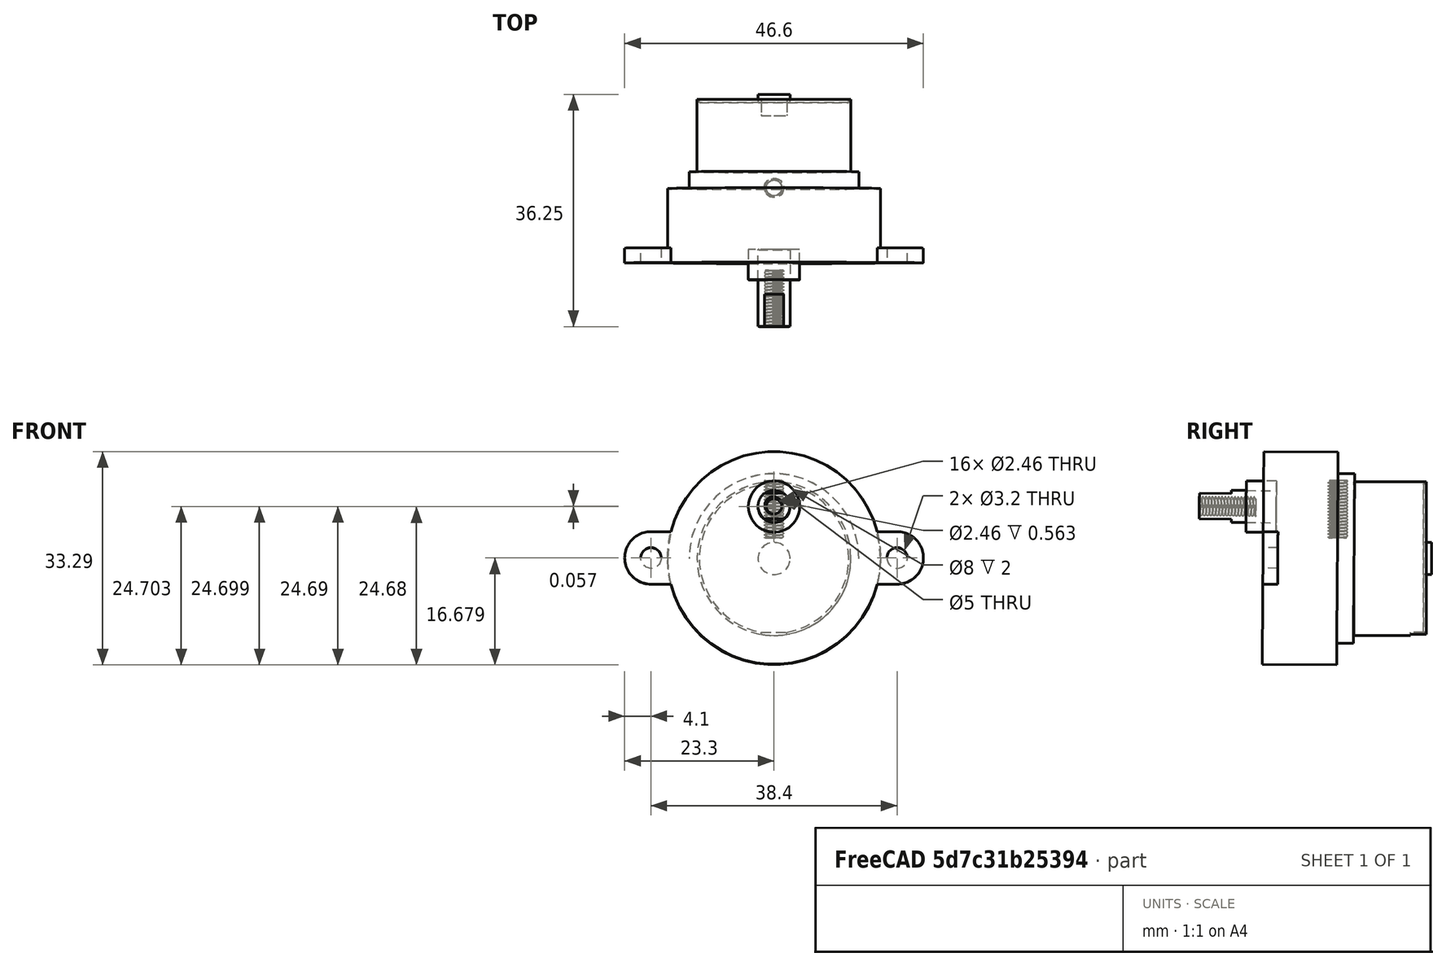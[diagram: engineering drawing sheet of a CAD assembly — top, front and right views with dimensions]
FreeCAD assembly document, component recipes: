
FREECAD ASSEMBLY — COMPONENT RECIPES ("JS30")

This assembly document has 4 components, labeled P0..P3 below (a component is one placed body or linked part). 4 of them carry a construction recipe — the FreeCAD feature program that regenerates the part from scratch, quoted from this document or its linked companion documents; the rest are supplied as boundary geometry only. No exploded tour is included for this assembly.
COMPONENT P0 — recipe-attached ("Motor", modeled in this document).
Construction recipe (the document's own serialized feature program — sketch geometry with constraints, then the solid features built on it; lengths are millimeters unless a unit is written):

FEATURE [Sketcher::SketchObject] Sketch
  ArcFitTolerance = 1e-06
  AttachmentSupport = -> [XZ_Plane]
  FullyConstrained = true
  MakeInternals = false
  MapMode = 5
  Placement = pos=(0,0,0) rot=(1,0,0;1.5708rad)
  sketch-geometry (1):
    g0: Circle CenterX=0 CenterY=0 CenterZ=0 NormalX=0 NormalY=0 NormalZ=1 AngleXU=0 Radius=12
  constraints (2):
    c: Diameter(g0) = 24
    c: Coincident(g0,g-1)
FEATURE [PartDesign::Pad] Pad
  Direction = (0,-1,2e-16)
  Length = 11.3
  Length2 = 10
  Placement = pos=(0,0,0) rot=(1,0,0;1.5708rad)
  Profile = -> Sketch [Edge1]
  ReferenceAxis = -> Sketch [N_Axis]
  Refine = true
  Reversed = true
  Suppressed = false
  Type = 0
FEATURE [Sketcher::SketchObject] Sketch001
  ArcFitTolerance = 1e-06
  AttachmentSupport = -> [Pad]
  FullyConstrained = true
  MakeInternals = false
  MapMode = 5
  Placement = pos=(0,11.3,0) rot=(-1,0,0;1.5708rad)
  sketch-geometry (1):
    g0: Circle CenterX=0 CenterY=0 CenterZ=0 NormalX=0 NormalY=0 NormalZ=1 AngleXU=0 Radius=11.65
  constraints (2):
    c: Diameter(g0) = 23.3
    c: Coincident(g0,g-1)
FEATURE [PartDesign::Pocket] Pocket
  BaseFeature = -> Pad
  Direction = (0,-1,-2e-16)
  Length = 0.5
  Length2 = 5
  Placement = pos=(0,0,0) rot=(1,0,0;1.5708rad)
  Profile = -> Sketch001
  ReferenceAxis = -> Sketch001 [N_Axis]
  Refine = true
  Suppressed = false
  Type = 0
FEATURE [Sketcher::SketchObject] Sketch004
  ArcFitTolerance = 1e-06
  AttachmentSupport = -> [Pocket]
  ExternalGeometry = -> [Pocket]
  FullyConstrained = true
  MakeInternals = false
  MapMode = 5
  Placement = pos=(0,11.3,0) rot=(-1,0,0;1.5708rad)
  sketch-geometry (6):
    g0: GeomPoint X=0 Y=12 Z=0
    g1: LineSegment StartX=0 StartY=12 StartZ=0 EndX=2 EndY=12 EndZ=0
    g2: GeomPoint X=2 Y=11.477 Z=0
    g3: LineSegment StartX=2 StartY=12 StartZ=0 EndX=2 EndY=11.477 EndZ=0
    g4: LineSegment StartX=2 StartY=11.477 StartZ=0 EndX=0 EndY=11.477 EndZ=0
    g5: LineSegment StartX=0 StartY=11.477 StartZ=0 EndX=0 EndY=12 EndZ=0
  constraints (14):
    c: PointOnObject(g0,g-3)
    c: PointOnObject(g0,g-2)
    c: PointOnObject(g2,g-4)
    c: DistanceX(g1,g1) = 2
    c: Horizontal(g1,g1)
    c: Vertical(g1,g2)
    c: Coincident(g1,g0)
    c: Coincident(g3,g1)
    c: Coincident(g3,g2)
    c: Coincident(g4,g2)
    c: PointOnObject(g4,g-2)
    c: Horizontal(g4)
    c: Coincident(g5,g4)
    c: Coincident(g5,g0)
FEATURE [PartDesign::Pocket] Pocket002
  BaseFeature = -> Pocket
  Direction = (0,-1,-2e-16)
  Length = 2.5
  Length2 = 5
  Placement = pos=(0,0,0) rot=(1,0,0;1.5708rad)
  Profile = -> Sketch004
  ReferenceAxis = -> Sketch004 [N_Axis]
  Refine = true
  Suppressed = false
  Type = 0
FEATURE [PartDesign::Mirrored] Mirrored001
  BaseFeature = -> Pocket002
  MirrorPlane = -> Sketch004 [V_Axis]
  Originals = -> [Pocket002]
  Placement = pos=(0,0,0) rot=(1,0,0;1.5708rad)
  Refine = true
  Suppressed = false
  TransformMode = 0
FEATURE [Sketcher::SketchObject] Sketch012
  ArcFitTolerance = 1e-06
  AttachmentSupport = -> [Pocket]
  FullyConstrained = true
  MakeInternals = false
  MapMode = 5
  Placement = pos=(0,10.8,0) rot=(-1,0,0;1.5708rad)
  sketch-geometry (1):
    g0: Circle CenterX=0 CenterY=0 CenterZ=0 NormalX=0 NormalY=0 NormalZ=1 AngleXU=0 Radius=2.5
  constraints (2):
    c: Diameter(g0) = 5
    c: Coincident(g0,g-1)
FEATURE [PartDesign::Pad] Pad006
  BaseFeature = -> Mirrored001
  Direction = (0,1,2e-16)
  Length = 1.3
  Length2 = 10
  Placement = pos=(0,0,0) rot=(1,0,0;1.5708rad)
  Profile = -> Sketch012 [Edge1]
  ReferenceAxis = -> Sketch012 [N_Axis]
  Refine = true
  Suppressed = false
  Type = 0
FEATURE [PartDesign::Body] Body  label="Motor"
  AllowCompound = false
  Group = -> [Sketch,Pad,Sketch001,Pocket,Sketch004,Pocket002,Mirrored001,Sketch012,Pad006]
  Origin = -> Origin
  Tip = -> Pad006
COMPONENT P1 — recipe-attached ("GearBox", modeled in this document).
Construction recipe (the document's own serialized feature program — sketch geometry with constraints, then the solid features built on it; lengths are millimeters unless a unit is written):

FEATURE [Sketcher::SketchObject] Sketch002
  ArcFitTolerance = 1e-06
  AttachmentSupport = -> [XZ_Plane001]
  FullyConstrained = true
  MakeInternals = false
  MapMode = 5
  Placement = pos=(0,0,0) rot=(1,0,0;1.5708rad)
  sketch-geometry (1):
    g0: Circle CenterX=0 CenterY=0 CenterZ=0 NormalX=0 NormalY=0 NormalZ=1 AngleXU=0 Radius=16.6
  constraints (2):
    c: Diameter(g0) = 33.2
    c: Coincident(g0,g-1)
FEATURE [PartDesign::Pad] Pad001
  Direction = (0,-1,2e-16)
  Length = 14.2
  Length2 = 10
  Placement = pos=(0,0,0) rot=(1,0,0;1.5708rad)
  Profile = -> Sketch002 [Edge1]
  ReferenceAxis = -> Sketch002 [N_Axis]
  Refine = true
  Suppressed = false
  Type = 0
FEATURE [Sketcher::SketchObject] Sketch003
  ArcFitTolerance = 1e-06
  AttachmentSupport = -> [XZ_Plane001]
  ExternalGeometry = -> [Pad001]
  FullyConstrained = true
  MakeInternals = false
  MapMode = 5
  Placement = pos=(0,0,0) rot=(1,0,0;1.5708rad)
  sketch-geometry (2):
    g0: Circle CenterX=0 CenterY=0 CenterZ=0 NormalX=0 NormalY=0 NormalZ=1 AngleXU=0 Radius=13.25
    g1: Circle CenterX=0 CenterY=0 CenterZ=0 NormalX=0 NormalY=0 NormalZ=1 AngleXU=0 Radius=16.6
  constraints (4):
    c: Diameter(g0) = 26.5
    c: Coincident(g0,g-1)
    c: Coincident(g1,g0)
    c: Equal(g1,g-3)
FEATURE [PartDesign::Pocket] Pocket001
  BaseFeature = -> Pad001
  Direction = (0,1,-2e-16)
  Length = 2.6
  Length2 = 5
  Placement = pos=(0,0,0) rot=(1,0,0;1.5708rad)
  Profile = -> Sketch003
  ReferenceAxis = -> Sketch003 [N_Axis]
  Refine = true
  Reversed = true
  Suppressed = false
  Type = 0
FEATURE [Sketcher::SketchObject] Sketch005
  ArcFitTolerance = 1e-06
  AttachmentSupport = -> [Pocket001]
  FullyConstrained = true
  MakeInternals = false
  MapMode = 5
  Placement = pos=(0,-14.2,0) rot=(1,0,0;1.5708rad)
  sketch-geometry (14):
    g0: ArcOfCircle CenterX=19.2 CenterY=0 CenterZ=0 NormalX=0 NormalY=0 NormalZ=1 AngleXU=0 Radius=4.1 StartAngle=4.71239 EndAngle=7.85398
    g1: Circle CenterX=19.2 CenterY=0 CenterZ=0 NormalX=0 NormalY=0 NormalZ=1 AngleXU=0 Radius=1.6
    g2: LineSegment [constr] StartX=0 StartY=0 StartZ=0 EndX=9.6 EndY=0 EndZ=0
    g3: LineSegment [constr] StartX=9.6 StartY=0 StartZ=0 EndX=9.6 EndY=4.1 EndZ=0
    g4: LineSegment [constr] StartX=9.6 StartY=4.1 StartZ=0 EndX=0 EndY=4.1 EndZ=0
    g5: LineSegment [constr] StartX=0 StartY=4.1 StartZ=0 EndX=0 EndY=0 EndZ=0
    g6: LineSegment [constr] StartX=0 StartY=0 StartZ=0 EndX=0 EndY=-4.1 EndZ=0
    g7: LineSegment [constr] StartX=0 StartY=-4.1 StartZ=0 EndX=9.6 EndY=-4.1 EndZ=0
    g8: LineSegment [constr] StartX=9.6 StartY=-4.1 StartZ=0 EndX=9.6 EndY=0 EndZ=0
    g9: LineSegment [constr] StartX=9.6 StartY=0 StartZ=0 EndX=0 EndY=0 EndZ=0
    g10: LineSegment [constr] StartX=9.6 StartY=0 StartZ=0 EndX=19.2 EndY=0 EndZ=0
    g11: LineSegment StartX=9.6 StartY=4.1 StartZ=0 EndX=9.6 EndY=-4.1 EndZ=0
    g12: LineSegment StartX=9.6 StartY=-4.1 StartZ=0 EndX=19.2 EndY=-4.1 EndZ=0
    g13: LineSegment StartX=19.2 StartY=4.1 StartZ=0 EndX=9.6 EndY=4.1 EndZ=0
  constraints (38):
    c: Angle(g0) = 3.14159
    c: Diameter(g1) = 3.2
    c: Coincident(g1,g0)
    c: Coincident(g2,g3)
    c: Coincident(g3,g4)
    c: Coincident(g4,g5)
    c: Coincident(g5,g2)
    c: Horizontal(g2)
    c: Horizontal(g4)
    c: Vertical(g3)
    c: Vertical(g5)
    c: Coincident(g2,g-1)
    c: Coincident(g6,g7)
    c: Coincident(g7,g8)
    c: Coincident(g8,g9)
    c: Coincident(g9,g6)
    c: Vertical(g6)
    c: Vertical(g8)
    c: Horizontal(g7)
    c: Horizontal(g9)
    c: Coincident(g6,g2)
    c: Equal(g6,g5)
    c: Equal(g4,g7)
    c: PointOnObject(g0,g-1)
    c: Coincident(g10,g2)
    c: Coincident(g10,g0)
    c: Equal(g10,g2)
    c: DistanceX(g4,g0) = 19.2
    c: Coincident(g11,g12)
    c: Coincident(g13,g11)
    c: Vertical(g11)
    c: Horizontal(g12)
    c: Horizontal(g13)
    c: Coincident(g11,g3)
    c: Coincident(g12,g0)
    c: DistanceY(g0,g0) = 8.2
    c: Coincident(g13,g0)
    c: Vertical(g0,g0)
FEATURE [Sketcher::SketchObject] Sketch009
  ArcFitTolerance = 1e-06
  AttachmentSupport = -> [Pocket001]
  FullyConstrained = true
  MakeInternals = false
  MapMode = 5
  Placement = pos=(0,-14.2,0) rot=(1,0,0;1.5708rad)
  sketch-geometry (2):
    g0: LineSegment [constr] StartX=0 StartY=0 StartZ=0 EndX=0 EndY=8 EndZ=0
    g1: Circle CenterX=0 CenterY=8 CenterZ=0 NormalX=0 NormalY=0 NormalZ=1 AngleXU=0 Radius=4
  constraints (5):
    c: Distance(g0) = 8
    c: Coincident(g0,g-1)
    c: PointOnObject(g0,g-2)
    c: Diameter(g1) = 8
    c: Coincident(g1,g0)
FEATURE [PartDesign::Pocket] Pocket004
  BaseFeature = -> Pocket001
  Direction = (0,1,-2e-16)
  Length = 2
  Length2 = 5
  Placement = pos=(0,0,0) rot=(1,0,0;1.5708rad)
  Profile = -> Sketch009
  ReferenceAxis = -> Sketch009 [N_Axis]
  Refine = true
  Suppressed = false
  Type = 0
FEATURE [PartDesign::Pad] Pad005
  BaseFeature = -> Pocket004
  Direction = (0,-1,2e-16)
  Length = 2.3
  Length2 = 10
  Placement = pos=(0,0,0) rot=(1,0,0;1.5708rad)
  Profile = -> Sketch005
  ReferenceAxis = -> Sketch005 [N_Axis]
  Refine = true
  Reversed = true
  Suppressed = false
  Type = 0
FEATURE [PartDesign::Mirrored] Mirrored
  BaseFeature = -> Pad005
  MirrorPlane = -> Sketch005 [V_Axis]
  Originals = -> [Pad005]
  Placement = pos=(0,0,0) rot=(1,0,0;1.5708rad)
  Refine = true
  Suppressed = false
  TransformMode = 0
FEATURE [PartDesign::Body] Body001  label="GearBox"
  AllowCompound = false
  Group = -> [Sketch002,Pad001,Sketch003,Pocket001,Sketch005,Sketch009,Pocket004,Pad005,Mirrored]
  Origin = -> Origin001
  Placement = pos=(-2e-16,0,-3e-16) rot=(-1,0,0;0.0076rad)
  Tip = -> Mirrored
COMPONENT P2 — recipe-attached ("Brushing", modeled in this document).
Construction recipe (the document's own serialized feature program — sketch geometry with constraints, then the solid features built on it; lengths are millimeters unless a unit is written):

FEATURE [Sketcher::SketchObject] Sketch006
  ArcFitTolerance = 1e-06
  AttachmentSupport = -> [XZ_Plane002]
  FullyConstrained = true
  MakeInternals = false
  MapMode = 5
  Placement = pos=(0,0,0) rot=(1,0,0;1.5708rad)
  sketch-geometry (2):
    g0: Circle CenterX=0 CenterY=0 CenterZ=0 NormalX=0 NormalY=0 NormalZ=1 AngleXU=0 Radius=2.5
    g1: Circle CenterX=0 CenterY=0 CenterZ=0 NormalX=0 NormalY=0 NormalZ=1 AngleXU=0 Radius=4
  constraints (4):
    c: Diameter(g0) = 5
    c: Coincident(g0,g-1)
    c: Diameter(g1) = 8
    c: Coincident(g1,g0)
FEATURE [PartDesign::Pad] Pad003
  Direction = (0,-1,2e-16)
  Length = 4.7
  Length2 = 10
  Placement = pos=(0,0,0) rot=(1,0,0;1.5708rad)
  Profile = -> Sketch006
  ReferenceAxis = -> Sketch006 [N_Axis]
  Refine = true
  Suppressed = false
  Type = 0
FEATURE [PartDesign::Body] Body002  label="Brushing"
  AllowCompound = false
  Group = -> [Sketch006,Pad003]
  Origin = -> Origin002
  Placement = pos=(-6e-15,-12.1388,8.09249) rot=(-1,0,0;0.0076rad)
  Tip = -> Pad003
COMPONENT P3 — recipe-attached ("Shaft", modeled in this document).
Construction recipe (the document's own serialized feature program — sketch geometry with constraints, then the solid features built on it; lengths are millimeters unless a unit is written):

FEATURE [Sketcher::SketchObject] Sketch010
  ArcFitTolerance = 1e-06
  AttachmentSupport = -> [XY_Plane005]
  FullyConstrained = true
  MakeInternals = false
  MapMode = 5
  sketch-geometry (1):
    g0: Circle CenterX=0 CenterY=-2.5 CenterZ=0 NormalX=0 NormalY=0 NormalZ=1 AngleXU=0 Radius=2.5
  constraints (3):
    c: Diameter(g0) = 5
    c: PointOnObject(g0,g-2)
    c: Tangent(g0,g-1)
FEATURE [PartDesign::Pad] Pad004
  Direction = (0,0,1)
  Length = 12
  Length2 = 10
  Profile = -> Sketch010
  ReferenceAxis = -> Sketch010 [N_Axis]
  Refine = true
  Suppressed = false
  Type = 0
FEATURE [PartDesign::Boolean] Boolean
  BaseFeature = -> Pad004
  Group = -> [ScrewTap]
  Placement = pos=(0,2.5,0) rot=(0,0,1;0rad)
  Refine = true
  Suppressed = false
  Type = 1
  UsePlacement = true
FEATURE [Sketcher::SketchObject] Sketch011
  ArcFitTolerance = 1e-06
  AttachmentSupport = -> [Boolean]
  FullyConstrained = true
  MakeInternals = false
  MapMode = 5
  Placement = pos=(0,2.5,12) rot=(0,0,1;0rad)
  sketch-geometry (14):
    g0: GeomPoint [constr] X=0 Y=-2.5 Z=0
    g1: LineSegment [constr] StartX=-2 StartY=-5 StartZ=0 EndX=2 EndY=-5 EndZ=0
    g2: LineSegment [constr] StartX=2 StartY=-5 StartZ=0 EndX=2 EndY=0 EndZ=0
    g3: LineSegment [constr] StartX=2 StartY=0 StartZ=0 EndX=-2 EndY=0 EndZ=0
    g4: LineSegment [constr] StartX=-2 StartY=0 StartZ=0 EndX=-2 EndY=-5 EndZ=0
    g5: GeomPoint [constr] X=0 Y=-2.5 Z=0
    g6: LineSegment StartX=-3 StartY=0 StartZ=0 EndX=-3 EndY=-5 EndZ=0
    g7: LineSegment StartX=-3 StartY=-5 StartZ=0 EndX=-2 EndY=-5 EndZ=0
    g8: LineSegment StartX=-2 StartY=-5 StartZ=0 EndX=-2 EndY=0 EndZ=0
    g9: LineSegment StartX=-2 StartY=0 StartZ=0 EndX=-3 EndY=0 EndZ=0
    g10: LineSegment StartX=2 StartY=0 StartZ=0 EndX=3 EndY=0 EndZ=0
    g11: LineSegment StartX=3 StartY=0 StartZ=0 EndX=3 EndY=-5 EndZ=0
    g12: LineSegment StartX=2 StartY=-5 StartZ=0 EndX=2 EndY=0 EndZ=0
    g13: LineSegment StartX=3 StartY=-5 StartZ=0 EndX=2 EndY=-5 EndZ=0
  constraints (36):
    c: PointOnObject(g0,g-2)
    c: Coincident(g1,g2)
    c: Coincident(g2,g3)
    c: Coincident(g3,g4)
    c: Coincident(g4,g1)
    c: Horizontal(g1)
    c: Horizontal(g3)
    c: Vertical(g2)
    c: Vertical(g4)
    c: Symmetric(g3,g1,g5)
    c: Distance(g2,g4) = 4
    c: Distance(g1,g3) = 5
    c: Coincident(g5,g0)
    c: PointOnObject(g2,g-1)
    c: Coincident(g6,g7)
    c: Coincident(g7,g8)
    c: Coincident(g8,g9)
    c: Coincident(g9,g6)
    c: Vertical(g6)
    c: Vertical(g8)
    c: Horizontal(g7)
    c: Horizontal(g9)
    c: DistanceX(g9,g9) = 1
    c: Equal(g2,g6)
    c: Coincident(g8,g3)
    c: Coincident(g11,g13)
    c: Coincident(g13,g12)
    c: Coincident(g12,g10)
    c: Coincident(g10,g11)
    c: Vertical(g11)
    c: Vertical(g12)
    c: Horizontal(g13)
    c: Horizontal(g10)
    c: Equal(g10,g9)
    c: Equal(g6,g11)
    c: Coincident(g2,g10)
FEATURE [PartDesign::Pocket] Pocket005
  BaseFeature = -> Boolean
  Direction = (0,0,-1)
  Length = 5
  Length2 = 5
  Placement = pos=(0,2.5,0) rot=(0,0,1;0rad)
  Profile = -> Sketch011
  ReferenceAxis = -> Sketch011 [N_Axis]
  Refine = true
  Suppressed = false
  Type = 0
FEATURE [PartDesign::Body] Body003  label="Shaft"
  AllowCompound = false
  Group = -> [Sketch010,Pad004,Boolean,Sketch011,Pocket005]
  Origin = -> Origin005
  Placement = pos=(-2.4e-15,-12.1388,8.09249) rot=(0.576856,-0.575398,0.579788;2.08854rad)
  Tip = -> Pocket005
PROVENANCE & LICENSES
A FreeCAD (.FCStd) document from a public repository crawl; recipes are the document's own serialized feature recipes (and, for linked parts, companion documents' recipes).
License: cc0-1.0.
